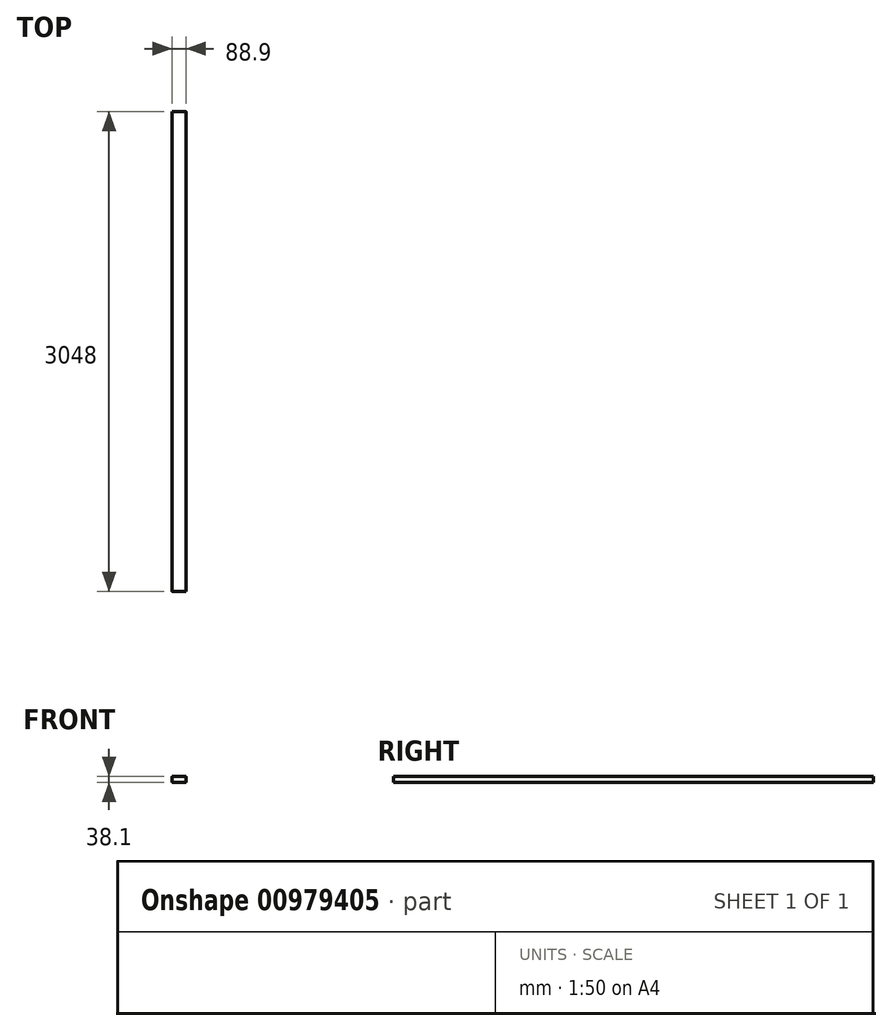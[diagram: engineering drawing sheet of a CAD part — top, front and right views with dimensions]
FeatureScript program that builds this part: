
annotation { "Feature Type Name" : "Feature", "Feature Type Description" : "" }
export const myFeature = defineFeature(function(context is Context, id is Id, definition is map)
    precondition{}
    {
        {
            var Q0;
            Q0=qCreatedBy(makeId("Front.planeOp"),FACE);
            var sketch = newSketch(context, id + "F0", { "sketchPlane" : qUnion([Q0])});
            skLineSegment(sketch, "E0.bottom", {"start": v(41.28, 19.05) * mm, "end": v(-41.28, 19.05) * mm});
            skLineSegment(sketch, "E0.top", {"start": v(41.28, -19.05) * mm, "end": v(-41.28, -19.05) * mm});
            skLineSegment(sketch, "E0.left", {"start": v(44.45, 15.88) * mm, "end": v(44.45, -15.88) * mm});
            skLineSegment(sketch, "E0.right", {"start": v(-44.45, 15.87) * mm, "end": v(-44.45, -15.88) * mm});
            skPoint(sketch, "E0.middle", {"position": v(0, 0) * mm});
            skPoint(sketch, "E1.visualSharp", {"position": v(-44.45, 19.05) * mm});
            skArc(sketch, "E1.filletArc", {"start": v(-41.28, 19.05) * mm, "mid": v(-43.52, 18.12) * mm, "end": v(-44.45, 15.87) * mm});
            skPoint(sketch, "E2.visualSharp", {"position": v(44.45, 19.05) * mm});
            skArc(sketch, "E2.filletArc", {"start": v(44.45, 15.88) * mm, "mid": v(43.52, 18.12) * mm, "end": v(41.28, 19.05) * mm});
            skPoint(sketch, "E3.visualSharp", {"position": v(44.45, -19.05) * mm});
            skArc(sketch, "E3.filletArc", {"start": v(41.28, -19.05) * mm, "mid": v(43.52, -18.12) * mm, "end": v(44.45, -15.88) * mm});
            skPoint(sketch, "E4.visualSharp", {"position": v(-44.45, -19.05) * mm});
            skArc(sketch, "E4.filletArc", {"start": v(-44.45, -15.88) * mm, "mid": v(-43.52, -18.12) * mm, "end": v(-41.28, -19.05) * mm});
            skSolve(sketch);
        }
        {
            var Q0;
            Q0=makeQuery(id+"F0.imprint","IMPRINT",FACE,{"disambiguationData":[TD([[makeQuery(id+"F0.imprint","IMPRINT",EDGE,{"derivedFrom":sQuery(id+"F0.wireOp",EDGE,"E0.bottom")}),1.0]])]});
            extrude(context, id + "F1", {"entities" : qUnion([Q0]), "oppositeDirection" : true, "depth" : 3048 * mm, "offsetDistance" : 25.4 * mm});
        }
    });
